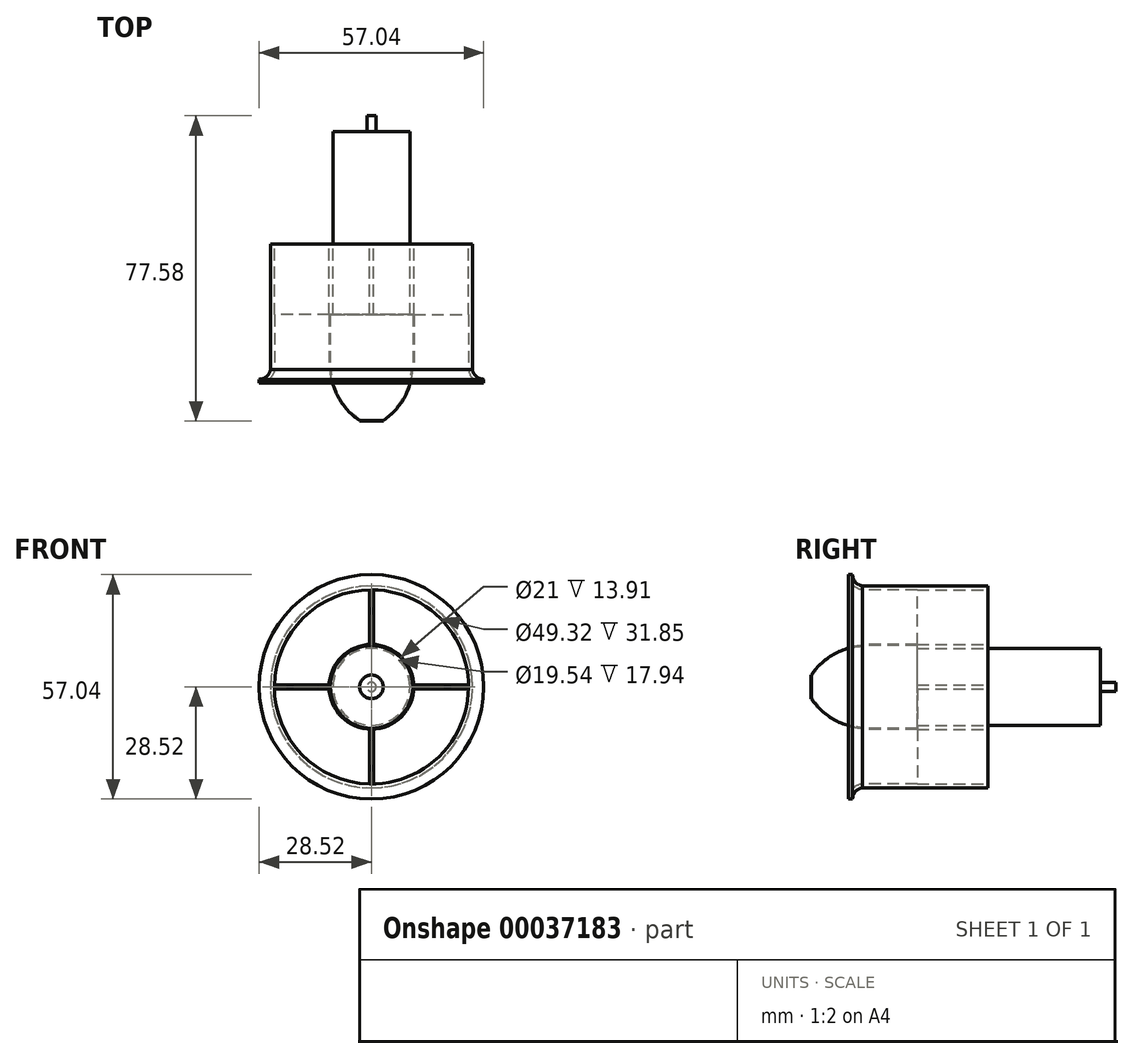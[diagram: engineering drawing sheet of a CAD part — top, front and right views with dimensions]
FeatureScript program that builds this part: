
annotation { "Feature Type Name" : "Feature", "Feature Type Description" : "" }
export const myFeature = defineFeature(function(context is Context, id is Id, definition is map)
    precondition{}
    {
        {
            var Q0;
            Q0=qCreatedBy(makeId("Front.planeOp"),FACE);
            var sketch = newSketch(context, id + "F0", { "sketchPlane" : qUnion([Q0])});
            skCircle(sketch, "E0", {"center": v(0, 0) * mm, "radius": 25.66 * mm});
            skCircle(sketch, "E1", {"center": v(0, 0) * mm, "radius": 24.66 * mm});
            skSolve(sketch);
        }
        {
            var Q0;
            Q0 = qSketchRegion(id + "F0", true);
            extrude(context, id + "F1", {"entities" : qUnion([Q0]), "oppositeDirection" : true, "depth" : (35.4 - 3.56) * mm});
        }
        {
            var Q0;
            Q0=qCreatedBy(makeId("Front.planeOp"),FACE);
            cPlane(context, id + "F2", {"entities" : qUnion([Q0]), "cplaneType" : CPlaneType.OFFSET, "offset" : 31.85 * mm, "oppositeDirection" : true, "width" : 150 * mm, "height" : 150 * mm});
        }
        {
            var Q0;
            Q0=qCreatedBy(id+"F2.planeOp",FACE);
            var sketch = newSketch(context, id + "F3", { "sketchPlane" : qUnion([Q0])});
            skCircle(sketch, "E2", {"center": v(0, 0) * mm, "radius": 9.77 * mm});
            skSolve(sketch);
        }
        {
            var Q0;
            Q0 = qSketchRegion(id + "F3", true);
            extrude(context, id + "F4", {"entities" : qUnion([Q0]), "oppositeDirection" : true, "depth" : 28.6 * mm});
        }
        {
            var Q0;
            Q0=qCreatedBy(makeId("Front.planeOp"),FACE);
            cPlane(context, id + "F5", {"entities" : qUnion([Q0]), "cplaneType" : CPlaneType.OFFSET, "offset" : 0 * mm, "width" : 150 * mm, "height" : 150 * mm});
        }
        {
            var Q0;
            Q0=qCreatedBy(id+"F5.planeOp",FACE);
            var sketch = newSketch(context, id + "F6", { "sketchPlane" : qUnion([Q0])});
            skCircle(sketch, "E3", {"center": v(0, 0) * mm, "radius": 28.52 * mm});
            skCircle(sketch, "E4.0", {"center": v(0, 0) * mm, "radius": 25.66 * mm});
            skSolve(sketch);
        }
        {
            var Q0;
            Q0=qCreatedBy(makeId("Right.planeOp"),FACE);
            var sketch = newSketch(context, id + "F7", { "sketchPlane" : qUnion([Q0])});
            skLineSegment(sketch, "E5.0", {"start": v(0, -28.52) * mm, "end": v(0, 25.66) * mm});
            skPoint(sketch, "E6.orphan", {"position": v(0, 28.52) * mm});
            skArc(sketch, "E7", {"start": v(-3.5, 28.52) * mm, "mid": v(-2.5, 25.92) * mm, "end": v(0, 24.66) * mm});
            skArc(sketch, "E8", {"start": v(-2.5, 28.52) * mm, "mid": v(-1.79, 26.62) * mm, "end": v(0, 25.66) * mm});
            skLineSegment(sketch, "E9", {"start": v(-3.5, 28.52) * mm, "end": v(-2.5, 28.52) * mm});
            skLineSegment(sketch, "E10", {"start": v(0, 25.66) * mm, "end": v(0, 24.66) * mm});
            skArc(sketch, "E11.MirrorCS", {"start": v(-3.5, -28.52) * mm, "mid": v(-2.5, -25.92) * mm, "end": v(0, -24.66) * mm});
            skArc(sketch, "E12.MirrorCS", {"start": v(-2.5, -28.52) * mm, "mid": v(-1.79, -26.62) * mm, "end": v(0, -25.66) * mm});
            skLineSegment(sketch, "E13.MirrorCS", {"start": v(-3.5, -28.52) * mm, "end": v(-2.5, -28.52) * mm});
            skLineSegment(sketch, "E14.MirrorCS", {"start": v(0, -25.66) * mm, "end": v(0, -24.66) * mm});
            skSolve(sketch);
        }
        {
            var Q0;
            Q0 = qSketchRegion(id + "F7", true);
            var Q1;
            Q1=sQuery(id+"F6.wireOp",EDGE,"E3");
            revolve(context, id + "F8", {"operationType" : NewBodyOperationType.ADD, "entities" : qUnion([Q0]), "axis" : qUnion([Q1]), "revolveType" : RevolveType.FULL});
        }
        {
            var Q0;
            Q0=qCreatedBy(makeId("Front.planeOp"),FACE);
            cPlane(context, id + "F9", {"entities" : qUnion([Q0]), "cplaneType" : CPlaneType.OFFSET, "offset" : 31.91 * mm, "oppositeDirection" : true, "width" : 150 * mm, "height" : 150 * mm});
        }
        {
            var Q0;
            Q0=qCreatedBy(id+"F9.planeOp",FACE);
            var sketch = newSketch(context, id + "F10", { "sketchPlane" : qUnion([Q0])});
            skLineSegment(sketch, "E15", {"start": v(-24.66, -0.5) * mm, "end": v(-24.66, 0.5) * mm});
            skLineSegment(sketch, "E16", {"start": v(-0.5, 24.66) * mm, "end": v(0.5, 24.66) * mm});
            skCircle(sketch, "E17.0", {"center": v(0, 0) * mm, "radius": 9.77 * mm});
            skArc(sketch, "E18.0", {"start": v(0.5, -10.76) * mm, "mid": v(7.62, -7.62) * mm, "end": v(10.76, -0.5) * mm});
            skLineSegment(sketch, "E19.trimOffspring", {"start": v(-10.76, 0.5) * mm, "end": v(-24.66, 0.5) * mm});
            skLineSegment(sketch, "E20.trimOffspring", {"start": v(-10.76, -0.5) * mm, "end": v(-24.66, -0.5) * mm});
            skLineSegment(sketch, "E21.trimOffspring", {"start": v(-0.5, 10.76) * mm, "end": v(-0.5, 24.66) * mm});
            skLineSegment(sketch, "E22.trimOffspring", {"start": v(0.5, 10.76) * mm, "end": v(0.5, 24.66) * mm});
            skLineSegment(sketch, "E23.trimOffspring", {"start": v(10.76, 0.5) * mm, "end": v(24.66, 0.5) * mm});
            skLineSegment(sketch, "E24.trimOffspring", {"start": v(10.76, -0.5) * mm, "end": v(24.66, -0.5) * mm});
            skLineSegment(sketch, "E25.trimOffspring", {"start": v(-0.5, -10.76) * mm, "end": v(-0.5, -24.66) * mm});
            skLineSegment(sketch, "E26.trimOffspring", {"start": v(0.5, -10.76) * mm, "end": v(0.5, -24.66) * mm});
            skLineSegment(sketch, "E27", {"start": v(-0.5, -24.66) * mm, "end": v(0.5, -24.66) * mm});
            skLineSegment(sketch, "E28", {"start": v(24.66, -0.5) * mm, "end": v(24.66, 0.5) * mm});
            skLineSegment(sketch, "E29", {"start": v(0.5, 24.66) * mm, "end": v(-0.5, 24.66) * mm});
            skArc(sketch, "E30.trimOffspring", {"start": v(-10.76, -0.5) * mm, "mid": v(-7.62, -7.62) * mm, "end": v(-0.5, -10.76) * mm});
            skArc(sketch, "E31.trimOffspring", {"start": v(-0.5, 10.76) * mm, "mid": v(-7.62, 7.62) * mm, "end": v(-10.76, 0.5) * mm});
            skArc(sketch, "E32.trimOffspring", {"start": v(10.76, 0.5) * mm, "mid": v(7.62, 7.62) * mm, "end": v(0.5, 10.76) * mm});
            skSolve(sketch);
        }
        {
            var Q0;
            Q0 = qSketchRegion(id + "F10", true);
            extrude(context, id + "F11", {"entities" : qUnion([Q0]), "operationType" : NewBodyOperationType.ADD, "depth" : 18 * mm});
        }
        {
            var Q0;
            Q0=qCreatedBy(makeId("Front.planeOp"),FACE);
            cPlane(context, id + "F12", {"entities" : qUnion([Q0]), "cplaneType" : CPlaneType.OFFSET, "offset" : 13 * mm, "width" : 150 * mm, "height" : 150 * mm});
        }
        {
            var Q0;
            Q0=qCreatedBy(id+"F12.planeOp",FACE);
            var sketch = newSketch(context, id + "F13", { "sketchPlane" : qUnion([Q0])});
            skCircle(sketch, "E33", {"center": v(0, 0) * mm, "radius": 3 * mm});
            skSolve(sketch);
        }
        {
            var Q0;
            Q0=qCreatedBy(makeId("Front.planeOp"),FACE);
            var sketch = newSketch(context, id + "F14", { "sketchPlane" : qUnion([Q0])});
            skCircle(sketch, "E34", {"center": v(0, 0) * mm, "radius": 10.5 * mm});
            skSolve(sketch);
        }
        {
            var Q0;
            Q0=qCreatedBy(makeId("Right.planeOp"),FACE);
            var sketch = newSketch(context, id + "F15", { "sketchPlane" : qUnion([Q0])});
            skArc(sketch, "E35", {"start": v(0, 10.5) * mm, "mid": v(-7.36, 8.24) * mm, "end": v(-13, 3) * mm});
            skArc(sketch, "E36.0", {"start": v(0.02, 10.25) * mm, "mid": v(-7.23, 8.02) * mm, "end": v(-12.8, 2.86) * mm});
            skLineSegment(sketch, "E37", {"start": v(-12.8, 2.86) * mm, "end": v(-13, 3) * mm});
            skLineSegment(sketch, "E38", {"start": v(0.02, 10.25) * mm, "end": v(0, 10.5) * mm});
            skSolve(sketch);
        }
        {
            var Q0;
            Q0 = qSketchRegion(id + "F15", true);
            var Q1;
            Q1=sQuery(id+"F14.wireOp",EDGE,"E34");
            revolve(context, id + "F16", {"entities" : qUnion([Q0]), "axis" : qUnion([Q1]), "revolveType" : RevolveType.FULL});
        }
        {
            var Q0;
            Q0 = qSketchRegion(id + "F13", true);
            extrude(context, id + "F17", {"entities" : qUnion([Q0]), "depth" : .125 * mm});
        }
        {
            var Q0;
            Q0=qCreatedBy(makeId("Front.planeOp"),FACE);
            var sketch = newSketch(context, id + "F18", { "sketchPlane" : qUnion([Q0])});
            skCircle(sketch, "E39.0", {"center": v(0, 0) * mm, "radius": 10.5 * mm});
            skArc(sketch, "E39.1", {"start": v(0.5, 10.76) * mm, "mid": v(-7.25, 7.96) * mm, "end": v(-10.76, 0.5) * mm});
            skArc(sketch, "E40.0", {"start": v(10.76, -0.5) * mm, "mid": v(7.96, 7.25) * mm, "end": v(0.5, 10.76) * mm});
            skArc(sketch, "E41.0", {"start": v(-10.76, 0.5) * mm, "mid": v(-7.62, -7.62) * mm, "end": v(0.5, -10.76) * mm});
            skArc(sketch, "E42.0", {"start": v(0.5, -10.76) * mm, "mid": v(7.62, -7.62) * mm, "end": v(10.76, -0.5) * mm});
            skPoint(sketch, "E43.orphan", {"position": v(-10.76, -0.5) * mm});
            skPoint(sketch, "E44.orphan", {"position": v(-0.5, 10.76) * mm});
            skPoint(sketch, "E45.orphan", {"position": v(10.76, 0.5) * mm});
            skArc(sketch, "E46.0", {"start": v(-0.5, 10.76) * mm, "mid": v(-7.62, 7.62) * mm, "end": v(-10.76, 0.5) * mm});
            skPoint(sketch, "E47.orphan", {"position": v(-0.5, -10.76) * mm});
            skSolve(sketch);
        }
        {
            var Q0;
            Q0 = qSketchRegion(id + "F18", true);
            var Q1;
            Q1=makeQuery(id+"F11.opExtrude","CAP_FACE",FACE,{"disambiguationData":[OSD([sQuery(id+"F10.wireOp",EDGE,"E15"),sQuery(id+"F10.wireOp",EDGE,"E17.0"),sQuery(id+"F10.wireOp",EDGE,"E18.0"),sQuery(id+"F10.wireOp",EDGE,"E19.trimOffspring"),sQuery(id+"F10.wireOp",EDGE,"E20.trimOffspring"),sQuery(id+"F10.wireOp",EDGE,"E21.trimOffspring"),sQuery(id+"F10.wireOp",EDGE,"E22.trimOffspring"),sQuery(id+"F10.wireOp",EDGE,"E23.trimOffspring"),sQuery(id+"F10.wireOp",EDGE,"E24.trimOffspring"),sQuery(id+"F10.wireOp",EDGE,"E25.trimOffspring"),sQuery(id+"F10.wireOp",EDGE,"E26.trimOffspring"),sQuery(id+"F10.wireOp",EDGE,"E27"),sQuery(id+"F10.wireOp",EDGE,"E28"),sQuery(id+"F10.wireOp",EDGE,"E29"),sQuery(id+"F10.wireOp",EDGE,"E30.trimOffspring"),sQuery(id+"F10.wireOp",EDGE,"E31.trimOffspring"),sQuery(id+"F10.wireOp",EDGE,"E32.trimOffspring")])],"isStart":false});
            extrude(context, id + "F19", {"entities" : qUnion([Q0]), "endBound" : BoundingType.UP_TO_SURFACE, "oppositeDirection" : true, "endBoundEntityFace" : qUnion([Q1]), "depth" : 18 * mm});
        }
        {
            var Q0;
            Q0=qCreatedBy(makeId("Front.planeOp"),FACE);
            cPlane(context, id + "F20", {"entities" : qUnion([Q0]), "cplaneType" : CPlaneType.OFFSET, "offset" : (31.85 + 28.6) * mm, "oppositeDirection" : true, "width" : 150 * mm, "height" : 150 * mm});
        }
        {
            var Q0;
            Q0=qCreatedBy(id+"F20.planeOp",FACE);
            var sketch = newSketch(context, id + "F21", { "sketchPlane" : qUnion([Q0])});
            skCircle(sketch, "E48", {"center": v(0, 0) * mm, "radius": 1.17 * mm});
            skSolve(sketch);
        }
        {
            var Q0;
            Q0 = qSketchRegion(id + "F21", true);
            extrude(context, id + "F22", {"entities" : qUnion([Q0]), "operationType" : NewBodyOperationType.ADD, "oppositeDirection" : true, "depth" : 4 * mm});
        }
    });
